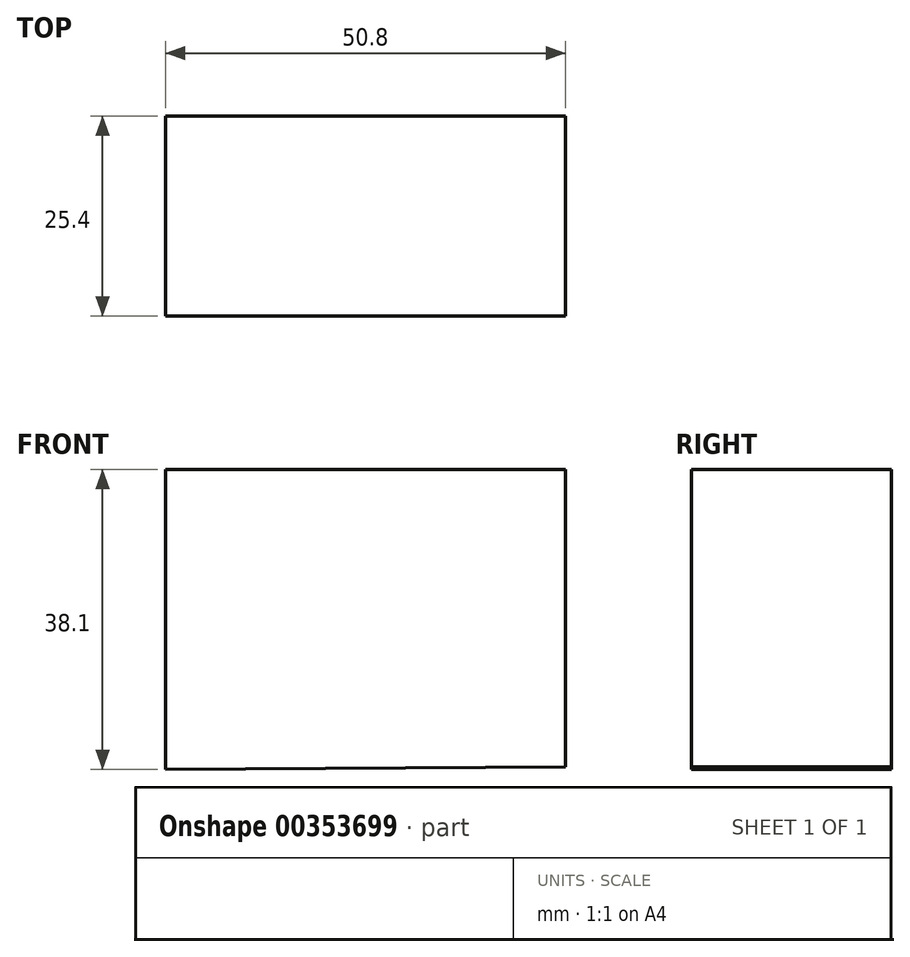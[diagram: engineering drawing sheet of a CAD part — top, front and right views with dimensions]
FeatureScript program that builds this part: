
annotation { "Feature Type Name" : "Feature", "Feature Type Description" : "" }
export const myFeature = defineFeature(function(context is Context, id is Id, definition is map)
    precondition{}
    {
        {
            var Q0;
            Q0=qCreatedBy(makeId("Front.planeOp"),FACE);
            var sketch = newSketch(context, id + "F0", { "sketchPlane" : qUnion([Q0])});
            skLineSegment(sketch, "E0", {"start": v(16.64, 9) * mm, "end": v(16.64, 47.1) * mm});
            skLineSegment(sketch, "E1", {"start": v(16.64, 47.1) * mm, "end": v(67.44, 47.1) * mm});
            skLineSegment(sketch, "E2", {"start": v(67.44, 47.1) * mm, "end": v(67.44, 9.31) * mm});
            skLineSegment(sketch, "E3", {"start": v(67.44, 9.31) * mm, "end": v(16.64, 9) * mm});
            skSolve(sketch);
        }
        {
            var Q0;
            Q0 = qSketchRegion(id + "F0", true);
            extrude(context, id + "F1", {"entities" : qUnion([Q0]), "depth" : 25.4 * mm});
        }
        {
            var Q0;
            Q0=makeQuery(id+"F1.opExtrude","CAP_FACE",FACE,{"disambiguationData":[OSD([sQuery(id+"F0.wireOp",EDGE,"E0"),sQuery(id+"F0.wireOp",EDGE,"E1"),sQuery(id+"F0.wireOp",EDGE,"E2"),sQuery(id+"F0.wireOp",EDGE,"E3")])],"isStart":false});
            var sketch = newSketch(context, id + "F2", { "sketchPlane" : qUnion([Q0])});
            skLineSegment(sketch, "E4", {"start": v(45.57, 47.1) * mm, "end": v(67.44, 24.09) * mm});
            skSolve(sketch);
        }
        {
            var Q0;
            {var subQ0=sQuery(id+"F2.wireOp",EDGE,"E4");Q0=makeQuery(id+"F2.imprint","IMPRINT",FACE,{"disambiguationData":[TD([[makeQuery(id+"F2.imprint","IMPRINT",EDGE,{"derivedFrom":subQ0}),1.0]])]});}
            extrude(context, id + "F3", {"entities" : qUnion([Q0]), "operationType" : NewBodyOperationType.REMOVE, "oppositeDirection" : true, "depth" : 31.75 * mm});
        }
        {
            var Q0;
            Q0 = qSketchRegion(id + "F0", true);
            extrude(context, id + "F4", {"entities" : qUnion([Q0]), "operationType" : NewBodyOperationType.ADD, "depth" : 25.4 * mm});
        }
    });
